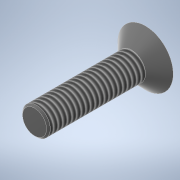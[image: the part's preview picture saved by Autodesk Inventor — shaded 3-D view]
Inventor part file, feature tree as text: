
AUTODESK INVENTOR PART (.ipt)
format: ipt  version: 2022 (Build 260153000, 153)  size: 175,104 bytes
history: native  units: in
note: dims shown in document units (in); Inventor stores cm internally (conversion verified against a paired STEP export)
features: sketch x2, revolve x1, chamfer x1, thread x1, extrude x1
ambient origin geometry x8: Origin, YZ Plane, XZ Plane, XY Plane, X Axis, Y Axis, Z Axis, Center Point
bodies: Body1 (feature_tree)
feature tree (6):
  revolve  "Revolution1"  [1 undecoded]
  chamfer  "Chamfer1"  Distance=0.1181in
  thread  "Thread1"  [1 undecoded]
  extrude  "Extrusion1"  Depth=0.0787in TaperAngle=45.0deg
  sketch  "Sketch1"  dims[d0=0.2362in d1=0.4724in]
  sketch  "Sketch2"  dims[d2=45.0deg d3=0.1181in d4=90.0deg d5=0.0079in d6=0.0787in d7=45.0deg d8=0.3268in d9=0.0in d10=0.0787in d11=0.0472in d12=0.0in]
note: 2 required parameter values undecoded (feature->parameter linkage not recoverable at this tier; creation-order binding heuristic only, values carry confidence <= 0.55)